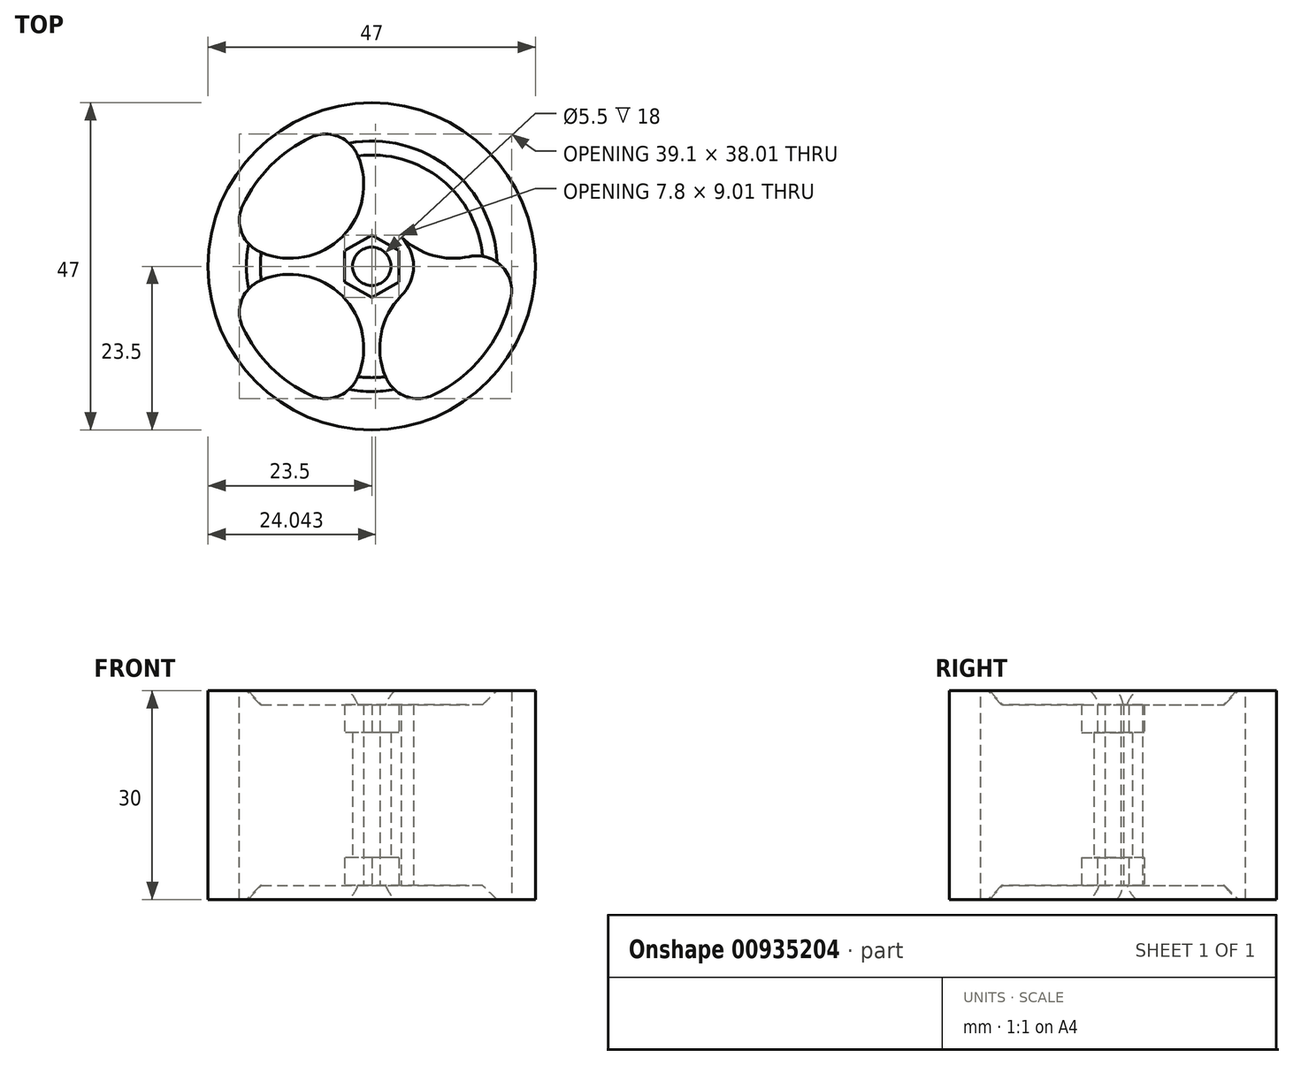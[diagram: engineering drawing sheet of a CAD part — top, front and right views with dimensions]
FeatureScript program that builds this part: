
annotation { "Feature Type Name" : "Feature", "Feature Type Description" : "" }
export const myFeature = defineFeature(function(context is Context, id is Id, definition is map)
    precondition{}
    {
        {
            var Q0;
            Q0=qCreatedBy(makeId("Top.planeOp"),FACE);
            var sketch = newSketch(context, id + "F0", { "sketchPlane" : qUnion([Q0])});
            skCircle(sketch, "E0", {"center": v(0, 0) * mm, "radius": 32.5 * mm});
            skCircle(sketch, "E1", {"center": v(0, 0) * mm, "radius": 22.5 * mm});
            skCircle(sketch, "E2", {"center": v(0, 0) * mm, "radius": 23.5 * mm});
            skCircle(sketch, "E3", {"center": v(0, 0) * mm, "radius": 20.5 * mm});
            skCircle(sketch, "E4", {"center": v(0, 0) * mm, "radius": 6 * mm});
            skArc(sketch, "E5", {"start": v(-19.88, 5) * mm, "mid": v(-4.24, 4.24) * mm, "end": v(-5, 19.88) * mm});
            skArc(sketch, "E6.MirrorCS", {"start": v(19.88, 5) * mm, "mid": v(4.24, 4.24) * mm, "end": v(5, 19.88) * mm});
            skArc(sketch, "E7.MirrorCS", {"start": v(19.88, -5) * mm, "mid": v(4.24, -4.24) * mm, "end": v(5, -19.88) * mm});
            skArc(sketch, "E8.MirrorCS", {"start": v(-19.88, -5) * mm, "mid": v(-4.24, -4.24) * mm, "end": v(-5, -19.88) * mm});
            skCircle(sketch, "E9.cCircle", {"center": v(0, 0) * mm, "radius": 3.9 * mm, "construction": true});
            skLineSegment(sketch, "E9.0", {"start": v(-3.9, -2.25) * mm, "end": v(-3.9, 2.25) * mm});
            skLineSegment(sketch, "E9.1", {"start": v(-3.9, 2.25) * mm, "end": v(0, 4.5) * mm});
            skLineSegment(sketch, "E9.2", {"start": v(0, 4.5) * mm, "end": v(3.9, 2.25) * mm});
            skLineSegment(sketch, "E9.3", {"start": v(3.9, 2.25) * mm, "end": v(3.9, -2.25) * mm});
            skLineSegment(sketch, "E9.4", {"start": v(3.9, -2.25) * mm, "end": v(0, -4.5) * mm});
            skLineSegment(sketch, "E9.5", {"start": v(0, -4.5) * mm, "end": v(-3.9, -2.25) * mm});
            skPoint(sketch, "E9.0.midPoint", {"position": v(-3.9, 0) * mm});
            skCircle(sketch, "E10", {"center": v(0, 0) * mm, "radius": 2.75 * mm});
            skCircle(sketch, "E11", {"center": v(0, 0) * mm, "radius": 3 * mm});
            skSolve(sketch);
        }
        {
            var Q0;
            {var subQ0=sQuery(id+"F0.wireOp",EDGE,"E5");var subQ1=sQuery(id+"F0.wireOp",EDGE,"E3");var subQ2=makeQuery(id+"F0.imprint","INTERSECT",VERTEX,{"disambiguationData":[OD(0.0)],"derivedFrom":[subQ1,subQ0]});Q0=makeQuery(id+"F0.imprint","IMPRINT",FACE,{"disambiguationData":[TD([[makeQuery(id+"F0.imprint","IMPRINT",EDGE,{"disambiguationData":[TD([[subQ2,-1.0]])],"derivedFrom":subQ1}),1.0]])]});}
            var Q1;
            Q1=makeQuery(id+"F0.imprint","IMPRINT",FACE,{"disambiguationData":[TD([[makeQuery(id+"F0.imprint","IMPRINT",EDGE,{"derivedFrom":sQuery(id+"F0.wireOp",EDGE,"E9.0")}),1.0]])]});
            var Q2;
            {var subQ0=sQuery(id+"F0.wireOp",EDGE,"E5");var subQ1=sQuery(id+"F0.wireOp",EDGE,"E3");var subQ2=makeQuery(id+"F0.imprint","INTERSECT",VERTEX,{"disambiguationData":[OD(1.0)],"derivedFrom":[subQ1,subQ0]});Q2=makeQuery(id+"F0.imprint","IMPRINT",FACE,{"disambiguationData":[TD([[makeQuery(id+"F0.imprint","IMPRINT",EDGE,{"disambiguationData":[TD([[subQ2,1.0]])],"derivedFrom":subQ1}),1.0]])]});}
            var Q3;
            {var subQ0=sQuery(id+"F0.wireOp",EDGE,"E6.MirrorCS");var subQ1=sQuery(id+"F0.wireOp",EDGE,"E3");var subQ2=makeQuery(id+"F0.imprint","INTERSECT",VERTEX,{"disambiguationData":[OD(0.0)],"derivedFrom":[subQ1,subQ0]});Q3=makeQuery(id+"F0.imprint","IMPRINT",FACE,{"disambiguationData":[TD([[makeQuery(id+"F0.imprint","IMPRINT",EDGE,{"disambiguationData":[TD([[subQ2,1.0]])],"derivedFrom":subQ1}),1.0]])]});}
            var Q4;
            {var subQ0=sQuery(id+"F0.wireOp",EDGE,"E7.MirrorCS");var subQ1=sQuery(id+"F0.wireOp",EDGE,"E3");var subQ2=makeQuery(id+"F0.imprint","INTERSECT",VERTEX,{"disambiguationData":[OD(1.0)],"derivedFrom":[subQ1,subQ0]});Q4=makeQuery(id+"F0.imprint","IMPRINT",FACE,{"disambiguationData":[TD([[makeQuery(id+"F0.imprint","IMPRINT",EDGE,{"disambiguationData":[TD([[subQ2,1.0]])],"derivedFrom":subQ1}),1.0]])]});}
            var Q5;
            Q5=makeQuery(id+"F0.imprint","IMPRINT",FACE,{"disambiguationData":[TD([[makeQuery(id+"F0.imprint","IMPRINT",EDGE,{"derivedFrom":sQuery(id+"F0.wireOp",EDGE,"E1")}),1.0]])]});
            var Q6;
            Q6=makeQuery(id+"F0.imprint","IMPRINT",FACE,{"disambiguationData":[TD([[makeQuery(id+"F0.imprint","IMPRINT",EDGE,{"derivedFrom":sQuery(id+"F0.wireOp",EDGE,"E1")}),-1.0]])]});
            var Q7;
            Q7=makeQuery(id+"F0.imprint","IMPRINT",FACE,{"disambiguationData":[TD([[makeQuery(id+"F0.imprint","IMPRINT",EDGE,{"derivedFrom":sQuery(id+"F0.wireOp",EDGE,"E9.0")}),-1.0]])]});
            extrude(context, id + "F1", {"entities" : qUnion([Q0, Q1, Q2, Q3, Q4, Q5, Q6, Q7]), "depth" : 30 * mm, "offsetDistance" : 25 * mm});
        }
        {
            var Q0;
            Q0=makeQuery(id+"F0.imprint","IMPRINT",FACE,{"disambiguationData":[TD([[makeQuery(id+"F0.imprint","IMPRINT",EDGE,{"derivedFrom":sQuery(id+"F0.wireOp",EDGE,"E10")}),-1.0]])]});
            extrude(context, id + "F2", {"entities" : qUnion([Q0]), "operationType" : NewBodyOperationType.ADD, "depth" : 28 * mm, "offsetDistance" : 25 * mm, "hasSecondDirection" : true, "secondDirectionOppositeDirection" : false, "secondDirectionDepth" : 2 * mm});
        }
        {
            var Q0;
            Q0=makeQuery(id+"F1.opExtrude","CAP_EDGE",EDGE,{"disambiguationData":[OSD([sQuery(id+"F0.wireOp",EDGE,"E11")])],"isStart":false});
            var Q1;
            Q1=makeQuery(id+"F1.opExtrude","CAP_EDGE",EDGE,{"disambiguationData":[OSD([sQuery(id+"F0.wireOp",EDGE,"E11")])],"isStart":true});
            chamfer(context, id + "F3", {"entities" : qUnion([Q0, Q1]), "width" : 15 * mm, "tangentPropagation" : true});
        }
        {
            var Q0;
            {var subQ0=sQuery(id+"F0.wireOp",EDGE,"E5");var subQ1=sQuery(id+"F0.wireOp",EDGE,"E3");Q0=makeQuery(id+"F1.opExtrude","SWEPT_EDGE",EDGE,{"disambiguationData":[OSD([subQ1,subQ0]),TDD([makeQuery(id+"F0.imprint","INTERSECT",VERTEX,{"disambiguationData":[OD(1.0)],"derivedFrom":[subQ1,subQ0]})])]});}
            var Q1;
            {var subQ0=sQuery(id+"F0.wireOp",EDGE,"E6.MirrorCS");var subQ1=sQuery(id+"F0.wireOp",EDGE,"E3");Q1=makeQuery(id+"F1.opExtrude","SWEPT_EDGE",EDGE,{"disambiguationData":[OSD([subQ1,subQ0]),TDD([makeQuery(id+"F0.imprint","INTERSECT",VERTEX,{"disambiguationData":[OD(1.0)],"derivedFrom":[subQ1,subQ0]})])]});}
            var Q2;
            {var subQ0=sQuery(id+"F0.wireOp",EDGE,"E6.MirrorCS");var subQ1=sQuery(id+"F0.wireOp",EDGE,"E3");Q2=makeQuery(id+"F1.opExtrude","SWEPT_EDGE",EDGE,{"disambiguationData":[OSD([subQ1,subQ0]),TDD([makeQuery(id+"F0.imprint","INTERSECT",VERTEX,{"disambiguationData":[OD(0.0)],"derivedFrom":[subQ1,subQ0]})])]});}
            var Q3;
            {var subQ0=sQuery(id+"F0.wireOp",EDGE,"E7.MirrorCS");var subQ1=sQuery(id+"F0.wireOp",EDGE,"E3");Q3=makeQuery(id+"F1.opExtrude","SWEPT_EDGE",EDGE,{"disambiguationData":[OSD([subQ1,subQ0]),TDD([makeQuery(id+"F0.imprint","INTERSECT",VERTEX,{"disambiguationData":[OD(0.0)],"derivedFrom":[subQ1,subQ0]})])]});}
            var Q4;
            {var subQ0=sQuery(id+"F0.wireOp",EDGE,"E7.MirrorCS");var subQ1=sQuery(id+"F0.wireOp",EDGE,"E3");Q4=makeQuery(id+"F1.opExtrude","SWEPT_EDGE",EDGE,{"disambiguationData":[OSD([subQ1,subQ0]),TDD([makeQuery(id+"F0.imprint","INTERSECT",VERTEX,{"disambiguationData":[OD(1.0)],"derivedFrom":[subQ1,subQ0]})])]});}
            var Q5;
            {var subQ0=sQuery(id+"F0.wireOp",EDGE,"E5");var subQ1=sQuery(id+"F0.wireOp",EDGE,"E3");Q5=makeQuery(id+"F1.opExtrude","SWEPT_EDGE",EDGE,{"disambiguationData":[OSD([subQ1,subQ0]),TDD([makeQuery(id+"F0.imprint","INTERSECT",VERTEX,{"disambiguationData":[OD(0.0)],"derivedFrom":[subQ1,subQ0]})])]});}
            var Q6;
            {var subQ0=sQuery(id+"F0.wireOp",EDGE,"E8.MirrorCS");var subQ1=sQuery(id+"F0.wireOp",EDGE,"E3");Q6=makeQuery(id+"F1.opExtrude","SWEPT_EDGE",EDGE,{"disambiguationData":[OSD([subQ1,subQ0]),TDD([makeQuery(id+"F0.imprint","INTERSECT",VERTEX,{"disambiguationData":[OD(0.0)],"derivedFrom":[subQ1,subQ0]})])]});}
            var Q7;
            {var subQ0=sQuery(id+"F0.wireOp",EDGE,"E8.MirrorCS");var subQ1=sQuery(id+"F0.wireOp",EDGE,"E3");Q7=makeQuery(id+"F1.opExtrude","SWEPT_EDGE",EDGE,{"disambiguationData":[OSD([subQ1,subQ0]),TDD([makeQuery(id+"F0.imprint","INTERSECT",VERTEX,{"disambiguationData":[OD(1.0)],"derivedFrom":[subQ1,subQ0]})])]});}
            fillet(context, id + "F4", {"entities" : qUnion([Q0, Q1, Q2, Q3, Q4, Q5, Q6, Q7]), "radius" : 5 * mm, "tangentPropagation" : true, "allowEdgeOverflow" : false});
        }
        {
            var Q0;
            Q0=makeQuery(id+"F0.imprint","IMPRINT",FACE,{"disambiguationData":[TD([[makeQuery(id+"F0.imprint","IMPRINT",EDGE,{"derivedFrom":sQuery(id+"F0.wireOp",EDGE,"E9.0")}),-1.0]])]});
            var Q1;
            Q1=makeQuery(id+"F0.imprint","IMPRINT",FACE,{"disambiguationData":[TD([[makeQuery(id+"F0.imprint","IMPRINT",EDGE,{"derivedFrom":sQuery(id+"F0.wireOp",EDGE,"E10")}),-1.0]])]});
            extrude(context, id + "F5", {"entities" : qUnion([Q0, Q1]), "operationType" : NewBodyOperationType.REMOVE, "depth" : 6 * mm, "offsetDistance" : 25 * mm});
        }
        {
            var Q0;
            Q0=makeQuery(id+"F0.imprint","IMPRINT",FACE,{"disambiguationData":[TD([[makeQuery(id+"F0.imprint","IMPRINT",EDGE,{"derivedFrom":sQuery(id+"F0.wireOp",EDGE,"E10")}),-1.0]])]});
            var Q1;
            Q1=makeQuery(id+"F0.imprint","IMPRINT",FACE,{"disambiguationData":[TD([[makeQuery(id+"F0.imprint","IMPRINT",EDGE,{"derivedFrom":sQuery(id+"F0.wireOp",EDGE,"E9.0")}),-1.0]])]});
            var Q2;
            Q2=makeQuery(id+"F2.opExtrude","CAP_FACE",FACE,{"disambiguationData":[OSD([sQuery(id+"F0.wireOp",EDGE,"E10"),sQuery(id+"F0.wireOp",EDGE,"E11")])],"isStart":false});
            extrude(context, id + "F6", {"entities" : qUnion([Q0, Q1]), "operationType" : NewBodyOperationType.REMOVE, "endBound" : BoundingType.UP_TO_SURFACE, "depth" : 25 * mm, "endBoundEntityFace" : qUnion([Q2]), "offsetDistance" : 25 * mm, "hasSecondDirection" : true, "secondDirectionOppositeDirection" : false, "secondDirectionDepth" : 24 * mm});
        }
    });
